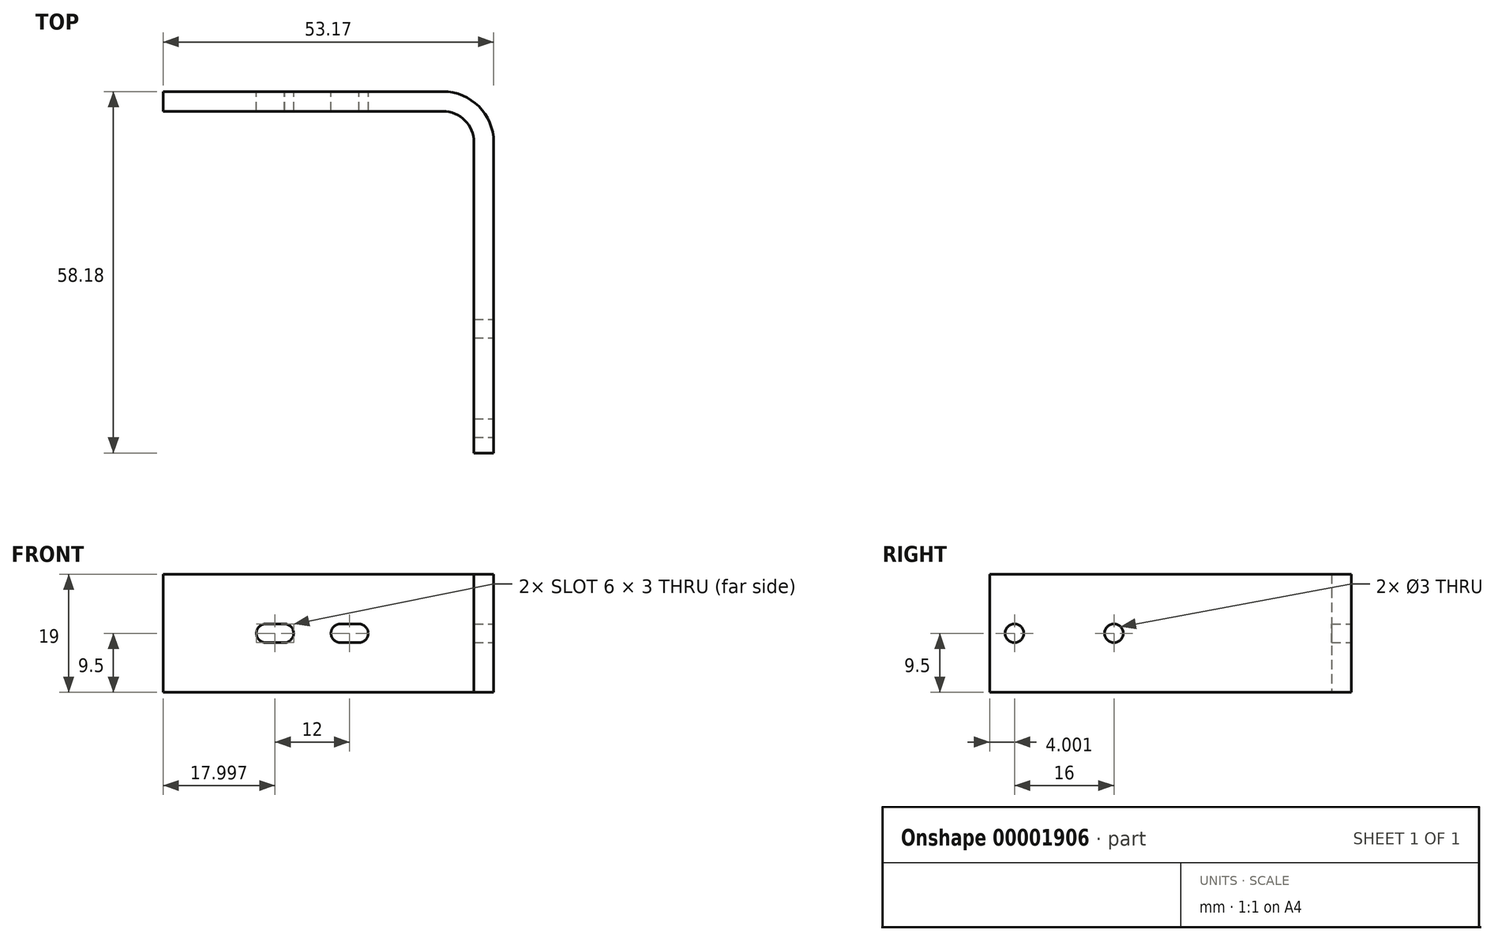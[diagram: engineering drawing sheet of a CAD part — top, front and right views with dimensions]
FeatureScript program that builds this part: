
annotation { "Feature Type Name" : "Feature", "Feature Type Description" : "" }
export const myFeature = defineFeature(function(context is Context, id is Id, definition is map)
    precondition{}
    {
        {
            var Q0;
            Q0=qCreatedBy(makeId("Top.planeOp"),FACE);
            var sketch = newSketch(context, id + "F0", { "sketchPlane" : qUnion([Q0])});
            skLineSegment(sketch, "E0", {"start": v(-16.17, 17.95) * mm, "end": v(28.83, 17.95) * mm});
            skLineSegment(sketch, "E1", {"start": v(33.83, 12.95) * mm, "end": v(33.83, -37.05) * mm});
            skPoint(sketch, "E2.visualSharp", {"position": v(33.83, 17.95) * mm});
            skArc(sketch, "E2.filletArc", {"start": v(33.83, 12.95) * mm, "mid": v(32.36, 16.49) * mm, "end": v(28.83, 17.95) * mm});
            skLineSegment(sketch, "E3.0", {"start": v(-16.17, 21.13) * mm, "end": v(28.83, 21.13) * mm});
            skArc(sketch, "E4.0", {"start": v(37, 12.95) * mm, "mid": v(34.6, 18.73) * mm, "end": v(28.83, 21.13) * mm});
            skLineSegment(sketch, "E5", {"start": v(-16.17, 21.13) * mm, "end": v(-16.17, 17.95) * mm});
            skLineSegment(sketch, "E6", {"start": v(33.83, -37.05) * mm, "end": v(37, -37.05) * mm});
            skLineSegment(sketch, "E7", {"start": v(37, 12.95) * mm, "end": v(37, -37.05) * mm});
            skSolve(sketch);
        }
        {
            var Q0;
            Q0=makeQuery(id+"F0.imprint","IMPRINT",FACE,{"disambiguationData":[TD([[makeQuery(id+"F0.imprint","IMPRINT",EDGE,{"derivedFrom":sQuery(id+"F0.wireOp",EDGE,"E0")}),1.0]])]});
            extrude(context, id + "F1", {"entities" : qUnion([Q0]), "depth" : 19 * mm});
        }
        {
            var Q0;
            Q0=makeQuery(id+"F1.opExtrude","SWEPT_FACE",FACE,{"disambiguationData":[OSD([sQuery(id+"F0.wireOp",EDGE,"E7")])]});
            var sketch = newSketch(context, id + "F2", { "sketchPlane" : qUnion([Q0])});
            skLineSegment(sketch, "E8.0", {"start": v(-37.05, 19) * mm, "end": v(-37.05, 0) * mm});
            skCircle(sketch, "E9", {"center": v(-33.05, 9.5) * mm, "radius": 1.5 * mm});
            skCircle(sketch, "E10", {"center": v(-17.05, 9.5) * mm, "radius": 1.5 * mm});
            skSolve(sketch);
        }
        {
            var Q0;
            Q0=makeQuery(id+"F2.imprint","IMPRINT",FACE,{"disambiguationData":[TD([[makeQuery(id+"F2.imprint","IMPRINT",EDGE,{"derivedFrom":sQuery(id+"F2.wireOp",EDGE,"E10")}),1.0]])]});
            var Q1;
            Q1=makeQuery(id+"F2.imprint","IMPRINT",FACE,{"disambiguationData":[TD([[makeQuery(id+"F2.imprint","IMPRINT",EDGE,{"derivedFrom":sQuery(id+"F2.wireOp",EDGE,"E9")}),1.0]])]});
            extrude(context, id + "F3", {"entities" : qUnion([Q0, Q1]), "operationType" : NewBodyOperationType.REMOVE, "oppositeDirection" : true, "depth" : 5 * mm});
        }
        {
            var Q0;
            Q0=makeQuery(id+"F1.opExtrude","SWEPT_FACE",FACE,{"disambiguationData":[OSD([sQuery(id+"F0.wireOp",EDGE,"E3.0")])]});
            var sketch = newSketch(context, id + "F4", { "sketchPlane" : qUnion([Q0])});
            skArc(sketch, "E11", {"start": v(-12.33, 8) * mm, "mid": v(-10.83, 9.5) * mm, "end": v(-12.33, 11) * mm});
            skArc(sketch, "E12", {"start": v(-0.33, 8) * mm, "mid": v(1.17, 9.5) * mm, "end": v(-0.33, 11) * mm});
            skArc(sketch, "E13", {"start": v(-15.3, 11) * mm, "mid": v(-16.83, 9.5) * mm, "end": v(-15.32, 8) * mm});
            skArc(sketch, "E14", {"start": v(-3.3, 11) * mm, "mid": v(-4.83, 9.49) * mm, "end": v(-3.28, 8) * mm});
            skLineSegment(sketch, "E15", {"start": v(-6.33, 0) * mm, "end": v(-6.33, 5.93) * mm});
            skLineSegment(sketch, "E16", {"start": v(-15.3, 11) * mm, "end": v(-12.33, 11) * mm});
            skLineSegment(sketch, "E17", {"start": v(-15.34, 8) * mm, "end": v(-12.33, 8) * mm});
            skLineSegment(sketch, "E18", {"start": v(-3.35, 11) * mm, "end": v(-0.33, 11) * mm});
            skLineSegment(sketch, "E19", {"start": v(-3.38, 8) * mm, "end": v(-0.33, 8) * mm});
            skSolve(sketch);
        }
        {
            var Q0;
            Q0=makeQuery(id+"F4.imprint","IMPRINT",FACE,{"disambiguationData":[TD([[makeQuery(id+"F4.imprint","IMPRINT",EDGE,{"derivedFrom":sQuery(id+"F4.wireOp",EDGE,"E11")}),1.0]])]});
            var Q1;
            Q1=makeQuery(id+"F4.imprint","IMPRINT",FACE,{"disambiguationData":[TD([[makeQuery(id+"F4.imprint","IMPRINT",EDGE,{"derivedFrom":sQuery(id+"F4.wireOp",EDGE,"E12")}),1.0]])]});
            extrude(context, id + "F5", {"entities" : qUnion([Q0, Q1]), "operationType" : NewBodyOperationType.REMOVE, "oppositeDirection" : true, "depth" : 5 * mm});
        }
    });
